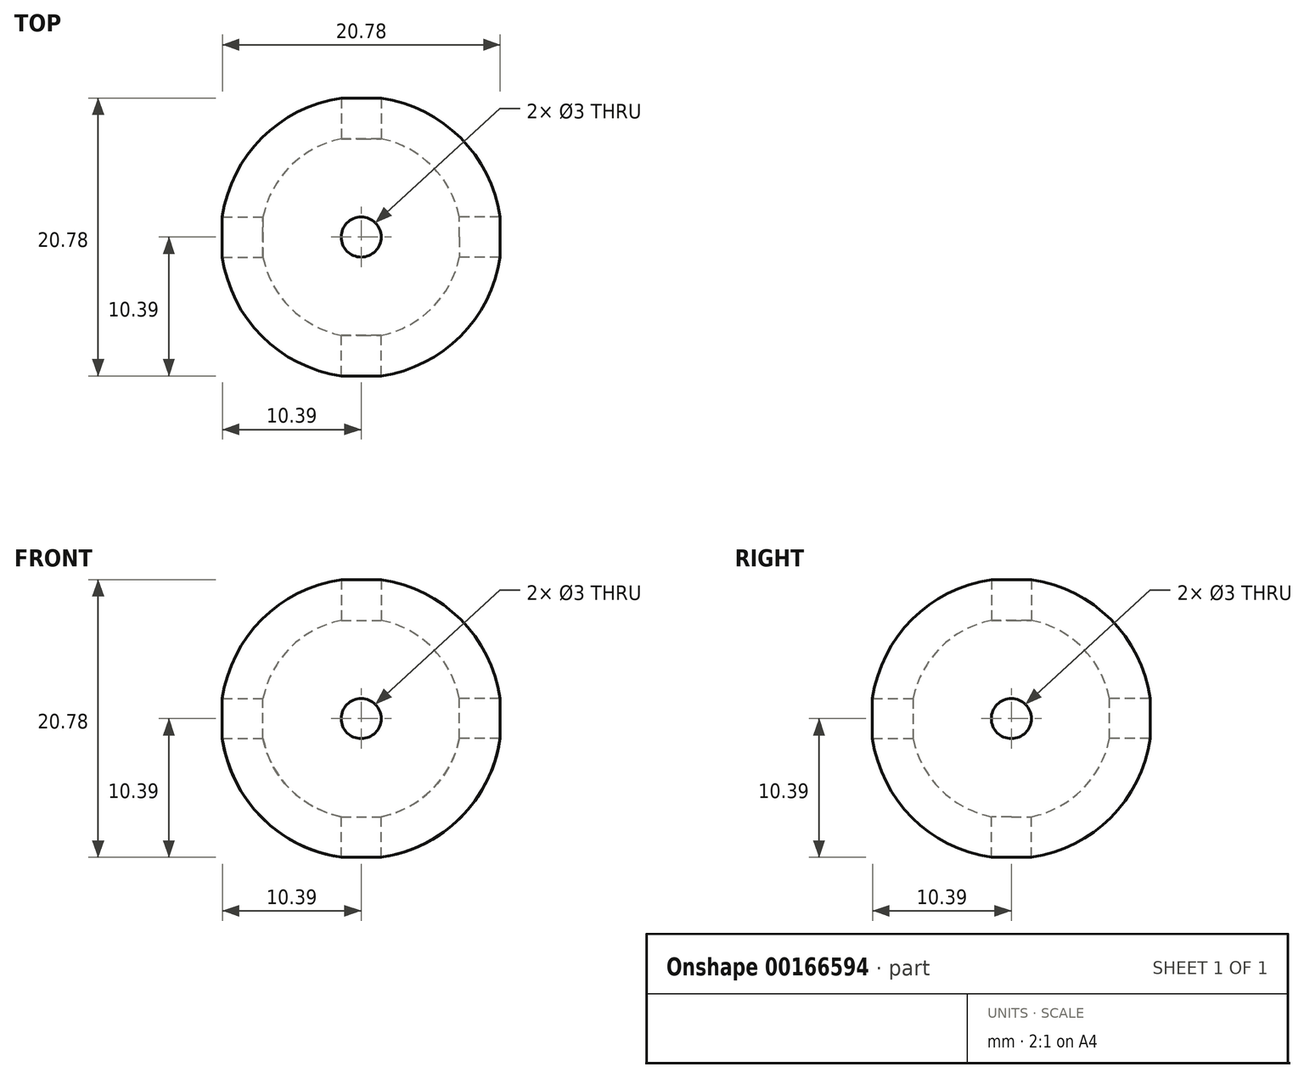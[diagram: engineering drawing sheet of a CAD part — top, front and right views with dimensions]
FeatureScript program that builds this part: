
annotation { "Feature Type Name" : "Feature", "Feature Type Description" : "" }
export const myFeature = defineFeature(function(context is Context, id is Id, definition is map)
    precondition{}
    {
        {
            var Q0;
            Q0=qCreatedBy(makeId("Top.planeOp"),FACE);
            var sketch = newSketch(context, id + "F0", { "sketchPlane" : qUnion([Q0])});
            skLineSegment(sketch, "E0", {"start": v(-12.35, 0) * mm, "end": v(13.15, 0) * mm});
            skArc(sketch, "E1", {"start": v(10.5, 0) * mm, "mid": v(0, 10.5) * mm, "end": v(-10.5, 0) * mm});
            skSolve(sketch);
        }
        {
            var Q0;
            {var subQ0=sQuery(id+"F0.wireOp",EDGE,"E1");Q0=makeQuery(id+"F0.imprint","IMPRINT",FACE,{"disambiguationData":[TD([[makeQuery(id+"F0.imprint","IMPRINT",EDGE,{"derivedFrom":subQ0}),1.0]])]});}
            var Q1;
            Q1=sQuery(id+"F0.wireOp",EDGE,"E0");
            revolve(context, id + "F1", {"entities" : qUnion([Q0]), "axis" : qUnion([Q1]), "revolveType" : RevolveType.FULL});
        }
        {
            var Q0;
            Q0=makeQuery(id+"F1.opRevolve","SWEPT_FACE",FACE,{"disambiguationData":[OSD([sQuery(id+"F0.wireOp",EDGE,"E1")])]});
            var Q1;
            Q1=makeQuery(id+"F1.opRevolve","SWEPT_BODY",BODY,{"disambiguationData":[OSD([sQuery(id+"F0.wireOp",EDGE,"E0"),sQuery(id+"F0.wireOp",EDGE,"E1")])]});
            shell(context, id + "F2", {"isHollow" : true, "entities" : qUnion([Q0]), "parts" : qUnion([Q1]), "thickness" : 3 * mm});
        }
        {
            var Q0;
            Q0=qCreatedBy(makeId("Top.planeOp"),FACE);
            var sketch = newSketch(context, id + "F3", { "sketchPlane" : qUnion([Q0])});
            skPoint(sketch, "E2", {"position": v(0, 0) * mm});
            skSolve(sketch);
        }
        {
            var Q0;
            Q0=sQuery(id+"F3.wireOp",VERTEX,"E2");
            var Q1;
            Q1=makeQuery(id+"F1.opRevolve","SWEPT_BODY",BODY,{"disambiguationData":[OSD([sQuery(id+"F0.wireOp",EDGE,"E0"),sQuery(id+"F0.wireOp",EDGE,"E1")])]});
            hole(context, id + "F4", {"style" : HoleStyle.SIMPLE, "endStyle" : HoleEndStyle.THROUGH, "holeDiameter" : 3 * mm, "locations" : qUnion([Q0]), "scope" : qUnion([Q1]), "isTappedThrough" : true});
        }
        {
            var Q0;
            Q0=qCreatedBy(makeId("Top.planeOp"),FACE);
            var sketch = newSketch(context, id + "F5", { "sketchPlane" : qUnion([Q0])});
            skPoint(sketch, "E3", {"position": v(0, 0) * mm});
            skSolve(sketch);
        }
        {
            var Q0;
            Q0=sQuery(id+"F5.wireOp",VERTEX,"E3");
            var Q1;
            Q1=makeQuery(id+"F1.opRevolve","SWEPT_BODY",BODY,{"disambiguationData":[OSD([sQuery(id+"F0.wireOp",EDGE,"E0"),sQuery(id+"F0.wireOp",EDGE,"E1")])]});
            hole(context, id + "F6", {"style" : HoleStyle.SIMPLE, "endStyle" : HoleEndStyle.THROUGH, "oppositeDirection" : true, "holeDiameter" : 3 * mm, "locations" : qUnion([Q0]), "scope" : qUnion([Q1]), "isTappedThrough" : true});
        }
        {
            var Q0;
            Q0=qCreatedBy(makeId("Right.planeOp"),FACE);
            var sketch = newSketch(context, id + "F7", { "sketchPlane" : qUnion([Q0])});
            skPoint(sketch, "E4", {"position": v(0, 0) * mm});
            skSolve(sketch);
        }
        {
            var Q0;
            Q0=sQuery(id+"F7.wireOp",VERTEX,"E4");
            var Q1;
            Q1=makeQuery(id+"F1.opRevolve","SWEPT_BODY",BODY,{"disambiguationData":[OSD([sQuery(id+"F0.wireOp",EDGE,"E0"),sQuery(id+"F0.wireOp",EDGE,"E1")])]});
            hole(context, id + "F8", {"style" : HoleStyle.SIMPLE, "endStyle" : HoleEndStyle.THROUGH, "holeDiameter" : 3 * mm, "locations" : qUnion([Q0]), "scope" : qUnion([Q1]), "isTappedThrough" : true});
        }
        {
            var Q0;
            Q0=qCreatedBy(makeId("Right.planeOp"),FACE);
            var sketch = newSketch(context, id + "F9", { "sketchPlane" : qUnion([Q0])});
            skPoint(sketch, "E5", {"position": v(0, 0) * mm});
            skSolve(sketch);
        }
        {
            var Q0;
            Q0=sQuery(id+"F9.wireOp",VERTEX,"E5");
            var Q1;
            Q1=makeQuery(id+"F1.opRevolve","SWEPT_BODY",BODY,{"disambiguationData":[OSD([sQuery(id+"F0.wireOp",EDGE,"E0"),sQuery(id+"F0.wireOp",EDGE,"E1")])]});
            hole(context, id + "F10", {"style" : HoleStyle.SIMPLE, "endStyle" : HoleEndStyle.THROUGH, "oppositeDirection" : true, "holeDiameter" : 3 * mm, "locations" : qUnion([Q0]), "scope" : qUnion([Q1]), "isTappedThrough" : true});
        }
        {
            var Q0;
            Q0=qCreatedBy(makeId("Front.planeOp"),FACE);
            var sketch = newSketch(context, id + "F11", { "sketchPlane" : qUnion([Q0])});
            skPoint(sketch, "E6", {"position": v(0, 0) * mm});
            skSolve(sketch);
        }
        {
            var Q0;
            Q0=sQuery(id+"F11.wireOp",VERTEX,"E6");
            var Q1;
            Q1=makeQuery(id+"F1.opRevolve","SWEPT_BODY",BODY,{"disambiguationData":[OSD([sQuery(id+"F0.wireOp",EDGE,"E0"),sQuery(id+"F0.wireOp",EDGE,"E1")])]});
            hole(context, id + "F12", {"style" : HoleStyle.SIMPLE, "endStyle" : HoleEndStyle.THROUGH, "holeDiameter" : 3 * mm, "locations" : qUnion([Q0]), "scope" : qUnion([Q1]), "isTappedThrough" : true});
        }
        {
            var Q0;
            Q0=qCreatedBy(makeId("Front.planeOp"),FACE);
            var sketch = newSketch(context, id + "F13", { "sketchPlane" : qUnion([Q0])});
            skPoint(sketch, "E7", {"position": v(0, 0) * mm});
            skSolve(sketch);
        }
        {
            var Q0;
            Q0=sQuery(id+"F13.wireOp",VERTEX,"E7");
            var Q1;
            Q1=makeQuery(id+"F1.opRevolve","SWEPT_BODY",BODY,{"disambiguationData":[OSD([sQuery(id+"F0.wireOp",EDGE,"E0"),sQuery(id+"F0.wireOp",EDGE,"E1")])]});
            hole(context, id + "F14", {"style" : HoleStyle.SIMPLE, "endStyle" : HoleEndStyle.THROUGH, "oppositeDirection" : true, "holeDiameter" : 3 * mm, "locations" : qUnion([Q0]), "scope" : qUnion([Q1]), "isTappedThrough" : true});
        }
    });
